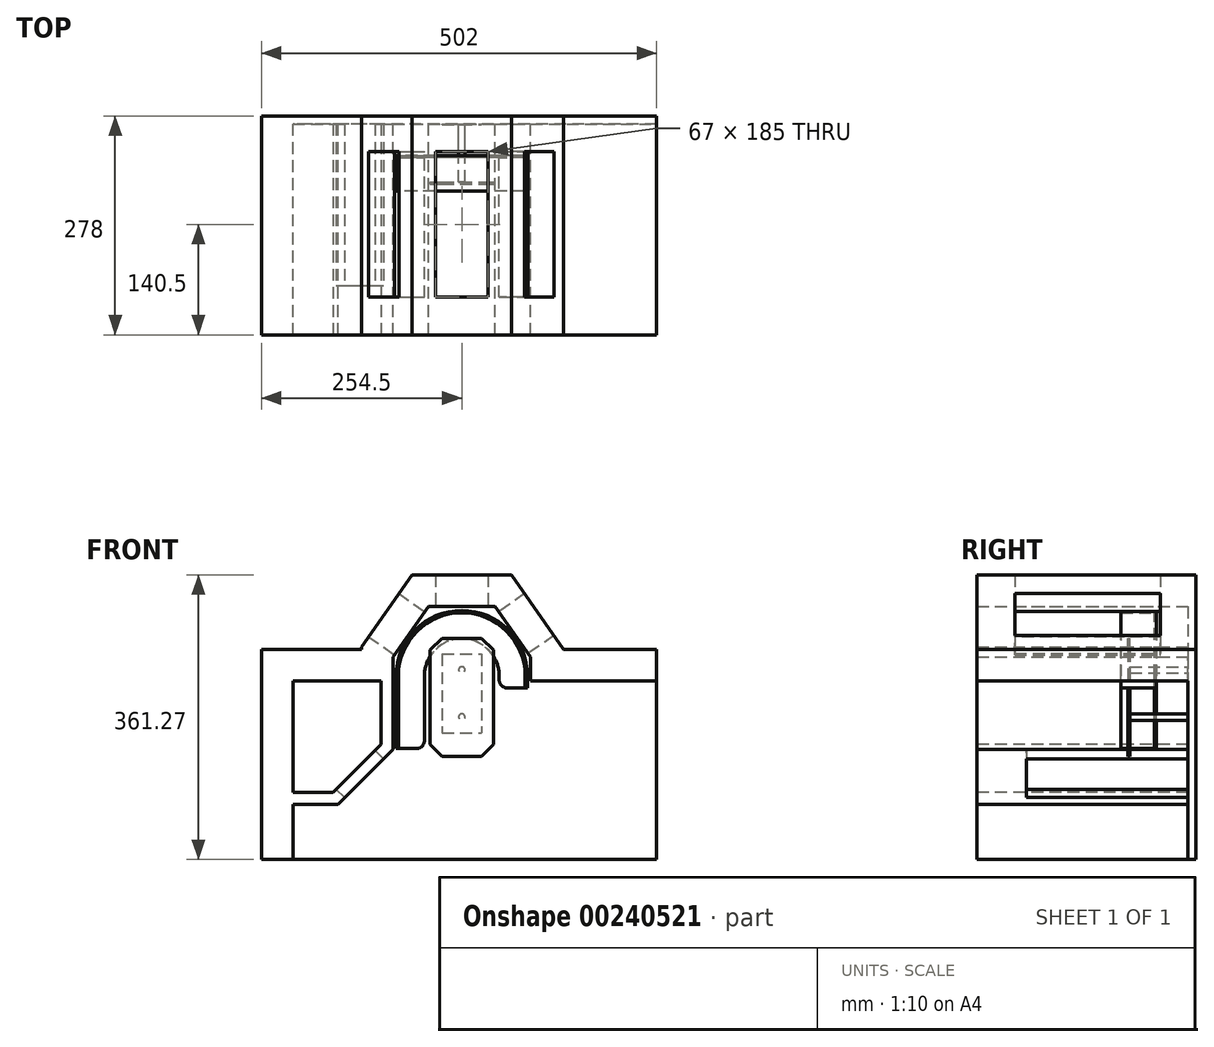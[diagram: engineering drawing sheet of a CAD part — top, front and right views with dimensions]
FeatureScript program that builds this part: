
annotation { "Feature Type Name" : "Feature", "Feature Type Description" : "" }
export const myFeature = defineFeature(function(context is Context, id is Id, definition is map)
    precondition{}
    {
        {
            var Q0;
            Q0=qCreatedBy(makeId("Front.planeOp"),FACE);
            var sketch = newSketch(context, id + "F0", { "sketchPlane" : qUnion([Q0])});
            skLineSegment(sketch, "E0", {"start": v(-214.5, -300.81) * mm, "end": v(-214.5, -230.81) * mm});
            skLineSegment(sketch, "E1", {"start": v(-214.5, -230.81) * mm, "end": v(-157.5, -230.81) * mm});
            skLineSegment(sketch, "E2", {"start": v(-87.5, -160.81) * mm, "end": v(-87.5, -43.81) * mm});
            skLineSegment(sketch, "E3", {"start": v(-87.5, -43.81) * mm, "end": v(-42.5, 20.46) * mm});
            skLineSegment(sketch, "E4", {"start": v(-42.5, 20.46) * mm, "end": v(42.5, 20.46) * mm});
            skLineSegment(sketch, "E5", {"start": v(42.5, 20.46) * mm, "end": v(87.5, -43.81) * mm});
            skLineSegment(sketch, "E6", {"start": v(87.5, -43.81) * mm, "end": v(87.5, -73.81) * mm});
            skLineSegment(sketch, "E7", {"start": v(87.5, -73.81) * mm, "end": v(247.5, -73.81) * mm});
            skLineSegment(sketch, "E8", {"start": v(247.5, -73.81) * mm, "end": v(247.5, -300.81) * mm});
            skLineSegment(sketch, "E9", {"start": v(247.5, -300.81) * mm, "end": v(-214.5, -300.81) * mm});
            skLineSegment(sketch, "E10", {"start": v(-157.5, -230.81) * mm, "end": v(-87.5, -160.81) * mm});
            skLineSegment(sketch, "E11", {"start": v(-63.32, 60.46) * mm, "end": v(63.32, 60.46) * mm, "construction": true});
            skLineSegment(sketch, "E12", {"start": v(63.32, 60.46) * mm, "end": v(154.9, -70.32) * mm, "construction": true});
            skLineSegment(sketch, "E13", {"start": v(-63.32, 60.46) * mm, "end": v(-114.5, -12.64) * mm, "construction": true});
            skSolve(sketch);
        }
        {
            var Q0;
            Q0 = qSketchRegion(id + "F0", true);
            extrude(context, id + "F1", {"entities" : qUnion([Q0]), "depth" : 10 * mm});
        }
        {
            var Q0;
            Q0=qCreatedBy(makeId("Front.planeOp"),FACE);
            var sketch = newSketch(context, id + "F2", { "sketchPlane" : qUnion([Q0])});
            skLineSegment(sketch, "E14.0", {"start": v(87.5, -73.81) * mm, "end": v(247.5, -73.81) * mm});
            skLineSegment(sketch, "E15.0", {"start": v(87.5, -43.81) * mm, "end": v(87.5, -73.81) * mm});
            skLineSegment(sketch, "E16.0", {"start": v(42.5, 20.46) * mm, "end": v(87.5, -43.81) * mm});
            skLineSegment(sketch, "E17.0", {"start": v(-42.5, 20.46) * mm, "end": v(42.5, 20.46) * mm});
            skLineSegment(sketch, "E18.0", {"start": v(-87.5, -43.81) * mm, "end": v(-42.5, 20.46) * mm});
            skLineSegment(sketch, "E19.0", {"start": v(-87.5, -160.81) * mm, "end": v(-87.5, -43.81) * mm});
            skLineSegment(sketch, "E20.0", {"start": v(-157.5, -230.81) * mm, "end": v(-87.5, -160.81) * mm});
            skLineSegment(sketch, "E21", {"start": v(-214.5, -215.81) * mm, "end": v(-163.71, -215.81) * mm});
            skLineSegment(sketch, "E22", {"start": v(-163.71, -215.81) * mm, "end": v(-127.5, -179.6) * mm});
            skLineSegment(sketch, "E23", {"start": v(-127.5, -179.6) * mm, "end": v(-127.5, -31.2) * mm});
            skLineSegment(sketch, "E24", {"start": v(-127.5, -31.2) * mm, "end": v(-63.32, 60.46) * mm});
            skLineSegment(sketch, "E25", {"start": v(-63.32, 60.46) * mm, "end": v(63.32, 60.46) * mm});
            skLineSegment(sketch, "E26", {"start": v(63.32, 60.46) * mm, "end": v(129.33, -33.81) * mm});
            skLineSegment(sketch, "E27", {"start": v(129.33, -33.81) * mm, "end": v(247.5, -33.81) * mm});
            skLineSegment(sketch, "E28", {"start": v(247.5, -33.81) * mm, "end": v(247.5, -73.81) * mm});
            skLineSegment(sketch, "E29.0", {"start": v(-214.5, -230.81) * mm, "end": v(-157.5, -230.81) * mm});
            skLineSegment(sketch, "E30", {"start": v(-214.5, -215.81) * mm, "end": v(-214.5, -230.81) * mm});
            skSolve(sketch);
        }
        {
            var Q0;
            Q0=makeQuery(id+"F2.imprint","IMPRINT",FACE,{"disambiguationData":[TD([[makeQuery(id+"F2.imprint","IMPRINT",EDGE,{"derivedFrom":sQuery(id+"F2.wireOp",EDGE,"E14.0")}),1.0]])]});
            extrude(context, id + "F3", {"entities" : qUnion([Q0]), "operationType" : NewBodyOperationType.ADD, "depth" : 278 * mm});
        }
        {
            var Q0;
            Q0=makeQuery(id+"F3.opExtrude","SWEPT_FACE",FACE,{"disambiguationData":[OSD([sQuery(id+"F2.wireOp",EDGE,"E17.0")])]});
            var sketch = newSketch(context, id + "F4", { "sketchPlane" : qUnion([Q0])});
            skLineSegment(sketch, "E31.bottom", {"start": v(-33.5, 230) * mm, "end": v(33.5, 230) * mm});
            skLineSegment(sketch, "E31.top", {"start": v(-33.5, 45) * mm, "end": v(33.5, 45) * mm});
            skLineSegment(sketch, "E31.left", {"start": v(-33.5, 230) * mm, "end": v(-33.5, 45) * mm});
            skLineSegment(sketch, "E31.right", {"start": v(33.5, 230) * mm, "end": v(33.5, 45) * mm});
            skSolve(sketch);
        }
        {
            var Q0;
            Q0=makeQuery(id+"F4.imprint","IMPRINT",FACE,{"disambiguationData":[TD([[makeQuery(id+"F4.imprint","IMPRINT",EDGE,{"derivedFrom":sQuery(id+"F4.wireOp",EDGE,"E31.bottom")}),-1.0]])]});
            extrude(context, id + "F5", {"entities" : qUnion([Q0]), "operationType" : NewBodyOperationType.REMOVE, "oppositeDirection" : true, "depth" : 50 * mm});
        }
        {
            var Q0;
            Q0=makeQuery(id+"F3.opExtrude","SWEPT_FACE",FACE,{"disambiguationData":[OSD([sQuery(id+"F2.wireOp",EDGE,"E18.0")])]});
            var sketch = newSketch(context, id + "F6", { "sketchPlane" : qUnion([Q0])});
            skLineSegment(sketch, "E32.bottom", {"start": v(-230, -82.62) * mm, "end": v(-45, -82.62) * mm});
            skLineSegment(sketch, "E32.top", {"start": v(-230, -15.62) * mm, "end": v(-45, -15.62) * mm});
            skLineSegment(sketch, "E32.left", {"start": v(-230, -82.62) * mm, "end": v(-230, -15.62) * mm});
            skLineSegment(sketch, "E32.right", {"start": v(-45, -82.62) * mm, "end": v(-45, -15.62) * mm});
            skSolve(sketch);
        }
        {
            var Q0;
            Q0=makeQuery(id+"F6.imprint","IMPRINT",FACE,{"disambiguationData":[TD([[makeQuery(id+"F6.imprint","IMPRINT",EDGE,{"derivedFrom":sQuery(id+"F6.wireOp",EDGE,"E32.bottom")}),1.0]])]});
            extrude(context, id + "F7", {"entities" : qUnion([Q0]), "operationType" : NewBodyOperationType.REMOVE, "oppositeDirection" : true, "depth" : 50 * mm});
        }
        {
            var Q0;
            Q0=makeQuery(id+"F3.opExtrude","SWEPT_FACE",FACE,{"disambiguationData":[OSD([sQuery(id+"F2.wireOp",EDGE,"E16.0")])]});
            var sketch = newSketch(context, id + "F8", { "sketchPlane" : qUnion([Q0])});
            skLineSegment(sketch, "E33.bottom", {"start": v(230, -15.62) * mm, "end": v(45, -15.62) * mm});
            skLineSegment(sketch, "E33.top", {"start": v(230, -80.62) * mm, "end": v(45, -80.62) * mm});
            skLineSegment(sketch, "E33.left", {"start": v(230, -15.62) * mm, "end": v(230, -80.62) * mm});
            skLineSegment(sketch, "E33.right", {"start": v(45, -15.62) * mm, "end": v(45, -80.62) * mm});
            skSolve(sketch);
        }
        {
            var Q0;
            Q0 = qSketchRegion(id + "F8", true);
            extrude(context, id + "F9", {"entities" : qUnion([Q0]), "operationType" : NewBodyOperationType.REMOVE, "oppositeDirection" : true, "depth" : 50 * mm});
        }
        {
            var Q0;
            Q0=makeQuery(id+"F3.opExtrude","CAP_FACE",FACE,{"disambiguationData":[OSD([sQuery(id+"F2.wireOp",EDGE,"E14.0"),sQuery(id+"F2.wireOp",EDGE,"E15.0"),sQuery(id+"F2.wireOp",EDGE,"E16.0"),sQuery(id+"F2.wireOp",EDGE,"E17.0"),sQuery(id+"F2.wireOp",EDGE,"E18.0"),sQuery(id+"F2.wireOp",EDGE,"E19.0"),sQuery(id+"F2.wireOp",EDGE,"E20.0"),sQuery(id+"F2.wireOp",EDGE,"E21"),sQuery(id+"F2.wireOp",EDGE,"E22"),sQuery(id+"F2.wireOp",EDGE,"E23"),sQuery(id+"F2.wireOp",EDGE,"E24"),sQuery(id+"F2.wireOp",EDGE,"E25"),sQuery(id+"F2.wireOp",EDGE,"E26"),sQuery(id+"F2.wireOp",EDGE,"E27"),sQuery(id+"F2.wireOp",EDGE,"E28"),sQuery(id+"F2.wireOp",EDGE,"E29.0"),sQuery(id+"F2.wireOp",EDGE,"E30")])],"isStart":false});
            var sketch = newSketch(context, id + "F10", { "sketchPlane" : qUnion([Q0])});
            skLineSegment(sketch, "E34", {"start": v(-127.5, -33.81) * mm, "end": v(-254.5, -33.81) * mm});
            skLineSegment(sketch, "E35", {"start": v(-254.5, -33.81) * mm, "end": v(-254.5, -300.65) * mm});
            skLineSegment(sketch, "E36.0", {"start": v(-214.5, -300.81) * mm, "end": v(-214.5, -230.81) * mm});
            skPoint(sketch, "E37.0", {"position": v(-214.5, -223.31) * mm});
            skLineSegment(sketch, "E38.0", {"start": v(-214.5, -215.81) * mm, "end": v(-163.71, -215.81) * mm});
            skLineSegment(sketch, "E39.0", {"start": v(-163.71, -215.81) * mm, "end": v(-127.5, -179.6) * mm});
            skLineSegment(sketch, "E40.0", {"start": v(-127.5, -179.6) * mm, "end": v(-127.5, -31.2) * mm});
            skLineSegment(sketch, "E41", {"start": v(-254.5, -300.65) * mm, "end": v(-214.5, -300.81) * mm});
            skSolve(sketch);
        }
        {
            var Q0;
            {var subQ2=sQuery(id+"F10.wireOp",EDGE,"E34");Q0=makeQuery(id+"F10.imprint","IMPRINT",FACE,{"disambiguationData":[TD([[makeQuery(id+"F10.imprint","IMPRINT",EDGE,{"derivedFrom":subQ2}),1.0]])]});}
            extrude(context, id + "F11", {"entities" : qUnion([Q0]), "operationType" : NewBodyOperationType.ADD, "oppositeDirection" : true, "depth" : 278 * mm});
        }
        {
            var Q0;
            {var subQ0=sQuery(id+"F2.wireOp",EDGE,"E30");Q0=makeQuery(id+"F11.boolean.opBoolean","MERGE",FACE,{"derivedFrom":[makeQuery(id+"F3.opExtrude","CAP_FACE",FACE,{"disambiguationData":[OSD([sQuery(id+"F2.wireOp",EDGE,"E14.0"),sQuery(id+"F2.wireOp",EDGE,"E15.0"),sQuery(id+"F2.wireOp",EDGE,"E16.0"),sQuery(id+"F2.wireOp",EDGE,"E17.0"),sQuery(id+"F2.wireOp",EDGE,"E18.0"),sQuery(id+"F2.wireOp",EDGE,"E19.0"),sQuery(id+"F2.wireOp",EDGE,"E20.0"),sQuery(id+"F2.wireOp",EDGE,"E21"),sQuery(id+"F2.wireOp",EDGE,"E22"),sQuery(id+"F2.wireOp",EDGE,"E23"),sQuery(id+"F2.wireOp",EDGE,"E24"),sQuery(id+"F2.wireOp",EDGE,"E25"),sQuery(id+"F2.wireOp",EDGE,"E26"),sQuery(id+"F2.wireOp",EDGE,"E27"),sQuery(id+"F2.wireOp",EDGE,"E28"),sQuery(id+"F2.wireOp",EDGE,"E29.0"),subQ0])],"isStart":false}),makeQuery(id+"F11.opExtrude","CAP_FACE",FACE,{"disambiguationData":[OSD([subQ0,sQuery(id+"F10.wireOp",EDGE,"E34"),sQuery(id+"F10.wireOp",EDGE,"E35"),sQuery(id+"F10.wireOp",EDGE,"E36.0"),sQuery(id+"F10.wireOp",EDGE,"E38.0"),sQuery(id+"F10.wireOp",EDGE,"E39.0"),sQuery(id+"F10.wireOp",EDGE,"E40.0"),sQuery(id+"F10.wireOp",EDGE,"E41")])],"isStart":true})]});}
            var sketch = newSketch(context, id + "F12", { "sketchPlane" : qUnion([Q0])});
            skLineSegment(sketch, "E42", {"start": v(-214.5, -215.81) * mm, "end": v(-163.71, -215.81) * mm});
            skLineSegment(sketch, "E43", {"start": v(-163.71, -215.81) * mm, "end": v(-102.5, -154.6) * mm});
            skLineSegment(sketch, "E44", {"start": v(-102.5, -154.6) * mm, "end": v(-102.5, -73.81) * mm});
            skLineSegment(sketch, "E45", {"start": v(-102.5, -73.81) * mm, "end": v(-214.5, -73.81) * mm});
            skLineSegment(sketch, "E46", {"start": v(-214.5, -73.81) * mm, "end": v(-214.5, -215.81) * mm});
            skSolve(sketch);
        }
        {
            var Q0;
            Q0=makeQuery(id+"F12.imprint","IMPRINT",FACE,{"disambiguationData":[TD([[makeQuery(id+"F12.imprint","IMPRINT",EDGE,{"derivedFrom":sQuery(id+"F12.wireOp",EDGE,"E42")}),1.0]])]});
            extrude(context, id + "F13", {"entities" : qUnion([Q0]), "operationType" : NewBodyOperationType.REMOVE, "oppositeDirection" : true, "depth" : 268 * mm});
        }
        {
            var Q0;
            Q0=makeQuery(id+"F3.opExtrude","SWEPT_FACE",FACE,{"disambiguationData":[OSD([sQuery(id+"F2.wireOp",EDGE,"E20.0")])]});
            var sketch = newSketch(context, id + "F14", { "sketchPlane" : qUnion([Q0])});
            skLineSegment(sketch, "E47.bottom", {"start": v(-10, -262.58) * mm, "end": v(-215, -262.58) * mm});
            skLineSegment(sketch, "E47.top", {"start": v(-10, -192.58) * mm, "end": v(-215, -192.58) * mm});
            skLineSegment(sketch, "E47.left", {"start": v(-10, -262.58) * mm, "end": v(-10, -192.58) * mm});
            skLineSegment(sketch, "E47.right", {"start": v(-215, -262.58) * mm, "end": v(-215, -192.58) * mm});
            skSolve(sketch);
        }
        {
            var Q0;
            Q0=makeQuery(id+"F14.imprint","IMPRINT",FACE,{"disambiguationData":[TD([[makeQuery(id+"F14.imprint","IMPRINT",EDGE,{"derivedFrom":sQuery(id+"F14.wireOp",EDGE,"E47.bottom")}),-1.0]])]});
            extrude(context, id + "F15", {"entities" : qUnion([Q0]), "operationType" : NewBodyOperationType.REMOVE, "oppositeDirection" : true, "depth" : 25 * mm});
        }
        {
            var Q0;
            Q0=makeQuery(id+"F15.boolean.opBoolean","MERGE",FACE,{"derivedFrom":[makeQuery(id+"F1.opExtrude","CAP_FACE",FACE,{"disambiguationData":[OSD([sQuery(id+"F0.wireOp",EDGE,"E0"),sQuery(id+"F0.wireOp",EDGE,"E1"),sQuery(id+"F0.wireOp",EDGE,"E2"),sQuery(id+"F0.wireOp",EDGE,"E3"),sQuery(id+"F0.wireOp",EDGE,"E4"),sQuery(id+"F0.wireOp",EDGE,"E5"),sQuery(id+"F0.wireOp",EDGE,"E6"),sQuery(id+"F0.wireOp",EDGE,"E7"),sQuery(id+"F0.wireOp",EDGE,"E8"),sQuery(id+"F0.wireOp",EDGE,"E9"),sQuery(id+"F0.wireOp",EDGE,"E10")])],"isStart":false}),makeQuery(id+"F13.boolean.opBoolean","COPY",FACE,{"derivedFrom":makeQuery(id+"F13.opExtrude","CAP_FACE",FACE,{"disambiguationData":[OSD([sQuery(id+"F12.wireOp",EDGE,"E42"),sQuery(id+"F12.wireOp",EDGE,"E43"),sQuery(id+"F12.wireOp",EDGE,"E44"),sQuery(id+"F12.wireOp",EDGE,"E45"),sQuery(id+"F12.wireOp",EDGE,"E46")])],"isStart":false})}),makeQuery(id+"F15.opExtrude","SWEPT_FACE",FACE,{"disambiguationData":[OSD([sQuery(id+"F14.wireOp",EDGE,"E47.left")])]})]});
            cPlane(context, id + "F16", {"entities" : qUnion([Q0]), "cplaneType" : CPlaneType.OFFSET, "offset" : 40 * mm, "width" : 150 * mm, "height" : 150 * mm});
        }
        {
            var Q0;
            Q0=qCreatedBy(id+"F16.planeOp",FACE);
            var sketch = newSketch(context, id + "F17", { "sketchPlane" : qUnion([Q0])});
            skArc(sketch, "E48", {"start": v(47.5, -68) * mm, "mid": v(0, -20.5) * mm, "end": v(-47.5, -68) * mm});
            skLineSegment(sketch, "E49", {"start": v(-83.5, -160) * mm, "end": v(-83.5, -68) * mm});
            skLineSegment(sketch, "E50", {"start": v(-47.5, -150) * mm, "end": v(-47.5, -68) * mm});
            skArc(sketch, "E51.trimOffspring", {"start": v(83.5, -68) * mm, "mid": v(0, 15.5) * mm, "end": v(-83.5, -68) * mm});
            skLineSegment(sketch, "E52", {"start": v(-83.5, -160) * mm, "end": v(-57.5, -160) * mm});
            skArc(sketch, "E53", {"start": v(-57.5, -160) * mm, "mid": v(-50.43, -157.07) * mm, "end": v(-47.5, -150) * mm});
            skLineSegment(sketch, "E54", {"start": v(83.5, -83) * mm, "end": v(83.5, -68) * mm});
            skLineSegment(sketch, "E55", {"start": v(83.5, -83) * mm, "end": v(57.5, -83) * mm});
            skLineSegment(sketch, "E56", {"start": v(47.5, -73) * mm, "end": v(47.5, -68) * mm});
            skPoint(sketch, "E57.visualSharp", {"position": v(47.5, -83) * mm});
            skArc(sketch, "E57.filletArc", {"start": v(47.5, -73) * mm, "mid": v(50.43, -80.07) * mm, "end": v(57.5, -83) * mm});
            skSolve(sketch);
        }
        {
            var Q0;
            Q0=makeQuery(id+"F17.imprint","IMPRINT",FACE,{"disambiguationData":[TD([[makeQuery(id+"F17.imprint","IMPRINT",EDGE,{"derivedFrom":sQuery(id+"F17.wireOp",EDGE,"E48")}),-1.0]])]});
            extrude(context, id + "F18", {"entities" : qUnion([Q0]), "depth" : 3 * mm});
        }
        {
            var Q0;
            Q0=makeQuery(id+"F18.opExtrude","CAP_FACE",FACE,{"disambiguationData":[OSD([sQuery(id+"F17.wireOp",EDGE,"E48"),sQuery(id+"F17.wireOp",EDGE,"E49"),sQuery(id+"F17.wireOp",EDGE,"E50"),sQuery(id+"F17.wireOp",EDGE,"Tax4DAiW-YkpO-NFdu-YiKu-K6yvG8vtNgXM"),sQuery(id+"F17.wireOp",EDGE,"PMcYtDSZ-tRXq-rbL0-rlYD-mqx147o4zxf1"),sQuery(id+"F17.wireOp",EDGE,"E51.trimOffspring")])],"isStart":false});
            var sketch = newSketch(context, id + "F19", { "sketchPlane" : qUnion([Q0])});
            skLineSegment(sketch, "E58.0", {"start": v(-83.5, -160) * mm, "end": v(-83.5, -68) * mm});
            skLineSegment(sketch, "E59.0", {"start": v(-83.5, -68) * mm, "end": v(-83.5, -68) * mm});
            skArc(sketch, "E60.0", {"start": v(80.5, -68) * mm, "mid": v(0, 12.5) * mm, "end": v(-80.5, -68) * mm});
            skLineSegment(sketch, "E60.1", {"start": v(-80.5, -160) * mm, "end": v(-80.5, -68) * mm});
            skLineSegment(sketch, "E61", {"start": v(-83.5, -160) * mm, "end": v(-80.5, -160) * mm});
            skArc(sketch, "E62.0", {"start": v(83.5, -68) * mm, "mid": v(0, 15.5) * mm, "end": v(-83.5, -68) * mm});
            skLineSegment(sketch, "E63", {"start": v(83.5, -68) * mm, "end": v(83.5, -83) * mm});
            skLineSegment(sketch, "E64", {"start": v(83.5, -83) * mm, "end": v(80.5, -83) * mm});
            skLineSegment(sketch, "E65", {"start": v(80.5, -83) * mm, "end": v(80.5, -68) * mm});
            skSolve(sketch);
        }
        {
            var Q0;
            Q0=makeQuery(id+"F19.imprint","IMPRINT",FACE,{"disambiguationData":[TD([[makeQuery(id+"F19.imprint","IMPRINT",EDGE,{"derivedFrom":sQuery(id+"F19.wireOp",EDGE,"E58.0")}),-1.0]])]});
            extrude(context, id + "F20", {"entities" : qUnion([Q0]), "operationType" : NewBodyOperationType.ADD, "depth" : 42 * mm});
        }
        {
            var Q0;
            Q0=makeQuery(id+"F15.boolean.opBoolean","MERGE",FACE,{"derivedFrom":[makeQuery(id+"F1.opExtrude","CAP_FACE",FACE,{"disambiguationData":[OSD([sQuery(id+"F0.wireOp",EDGE,"E0"),sQuery(id+"F0.wireOp",EDGE,"E1"),sQuery(id+"F0.wireOp",EDGE,"E2"),sQuery(id+"F0.wireOp",EDGE,"E3"),sQuery(id+"F0.wireOp",EDGE,"E4"),sQuery(id+"F0.wireOp",EDGE,"E5"),sQuery(id+"F0.wireOp",EDGE,"E6"),sQuery(id+"F0.wireOp",EDGE,"E7"),sQuery(id+"F0.wireOp",EDGE,"E8"),sQuery(id+"F0.wireOp",EDGE,"E9"),sQuery(id+"F0.wireOp",EDGE,"E10")])],"isStart":false}),makeQuery(id+"F13.boolean.opBoolean","COPY",FACE,{"derivedFrom":makeQuery(id+"F13.opExtrude","CAP_FACE",FACE,{"disambiguationData":[OSD([sQuery(id+"F12.wireOp",EDGE,"E42"),sQuery(id+"F12.wireOp",EDGE,"E43"),sQuery(id+"F12.wireOp",EDGE,"E44"),sQuery(id+"F12.wireOp",EDGE,"E45"),sQuery(id+"F12.wireOp",EDGE,"E46")])],"isStart":false})}),makeQuery(id+"F15.opExtrude","SWEPT_FACE",FACE,{"disambiguationData":[OSD([sQuery(id+"F14.wireOp",EDGE,"E47.left")])]})]});
            var sketch = newSketch(context, id + "F21", { "sketchPlane" : qUnion([Q0])});
            skLineSegment(sketch, "E66.bottom", {"start": v(-25, -40) * mm, "end": v(25, -40) * mm});
            skLineSegment(sketch, "E66.top", {"start": v(-25, -140) * mm, "end": v(25, -140) * mm});
            skLineSegment(sketch, "E66.left", {"start": v(-25, -40) * mm, "end": v(-25, -140) * mm});
            skLineSegment(sketch, "E66.right", {"start": v(25, -40) * mm, "end": v(25, -140) * mm});
            skSolve(sketch);
        }
        {
            var Q0;
            Q0=makeQuery(id+"F21.imprint","IMPRINT",FACE,{"disambiguationData":[TD([[makeQuery(id+"F21.imprint","IMPRINT",EDGE,{"derivedFrom":sQuery(id+"F21.wireOp",EDGE,"E66.bottom")}),-1.0]])]});
            extrude(context, id + "F22", {"entities" : qUnion([Q0]), "operationType" : NewBodyOperationType.ADD, "depth" : 0.5 * mm});
        }
        {
            var Q0;
            Q0=makeQuery(id+"F22.opExtrude","CAP_FACE",FACE,{"disambiguationData":[OSD([sQuery(id+"F21.wireOp",EDGE,"E66.bottom"),sQuery(id+"F21.wireOp",EDGE,"E66.top"),sQuery(id+"F21.wireOp",EDGE,"E66.left"),sQuery(id+"F21.wireOp",EDGE,"E66.right")])],"isStart":false});
            var sketch = newSketch(context, id + "F23", { "sketchPlane" : qUnion([Q0])});
            skCircle(sketch, "E67", {"center": v(0, -60) * mm, "radius": 4 * mm});
            skCircle(sketch, "E68", {"center": v(0, -120) * mm, "radius": 4 * mm});
            skSolve(sketch);
        }
        {
            var Q0;
            Q0 = qSketchRegion(id + "F23", true);
            extrude(context, id + "F24", {"entities" : qUnion([Q0]), "operationType" : NewBodyOperationType.ADD, "depth" : 73 * mm});
        }
        {
            var Q0;
            Q0=makeQuery(id+"F24.opExtrude","CAP_FACE",FACE,{"disambiguationData":[OSD([sQuery(id+"F23.wireOp",EDGE,"E67")])],"isStart":false});
            var sketch = newSketch(context, id + "F25", { "sketchPlane" : qUnion([Q0])});
            skLineSegment(sketch, "E69.bottom", {"start": v(-25, -20) * mm, "end": v(25, -20) * mm});
            skLineSegment(sketch, "E69.top", {"start": v(-25, -170) * mm, "end": v(25, -170) * mm});
            skLineSegment(sketch, "E69.left", {"start": v(-40, -35) * mm, "end": v(-40, -155) * mm});
            skLineSegment(sketch, "E69.right", {"start": v(40, -35) * mm, "end": v(40, -155) * mm});
            skLineSegment(sketch, "E70", {"start": v(-40, -35) * mm, "end": v(-25, -20) * mm});
            skLineSegment(sketch, "E71", {"start": v(25, -20) * mm, "end": v(40, -35) * mm});
            skLineSegment(sketch, "E72", {"start": v(-40, -155) * mm, "end": v(-25, -170) * mm});
            skLineSegment(sketch, "E73", {"start": v(25, -170) * mm, "end": v(40, -155) * mm});
            skSolve(sketch);
        }
        {
            var Q0;
            Q0 = qSketchRegion(id + "F25", true);
            extrude(context, id + "F26", {"entities" : qUnion([Q0]), "operationType" : NewBodyOperationType.ADD, "depth" : 3 * mm});
        }
    });
